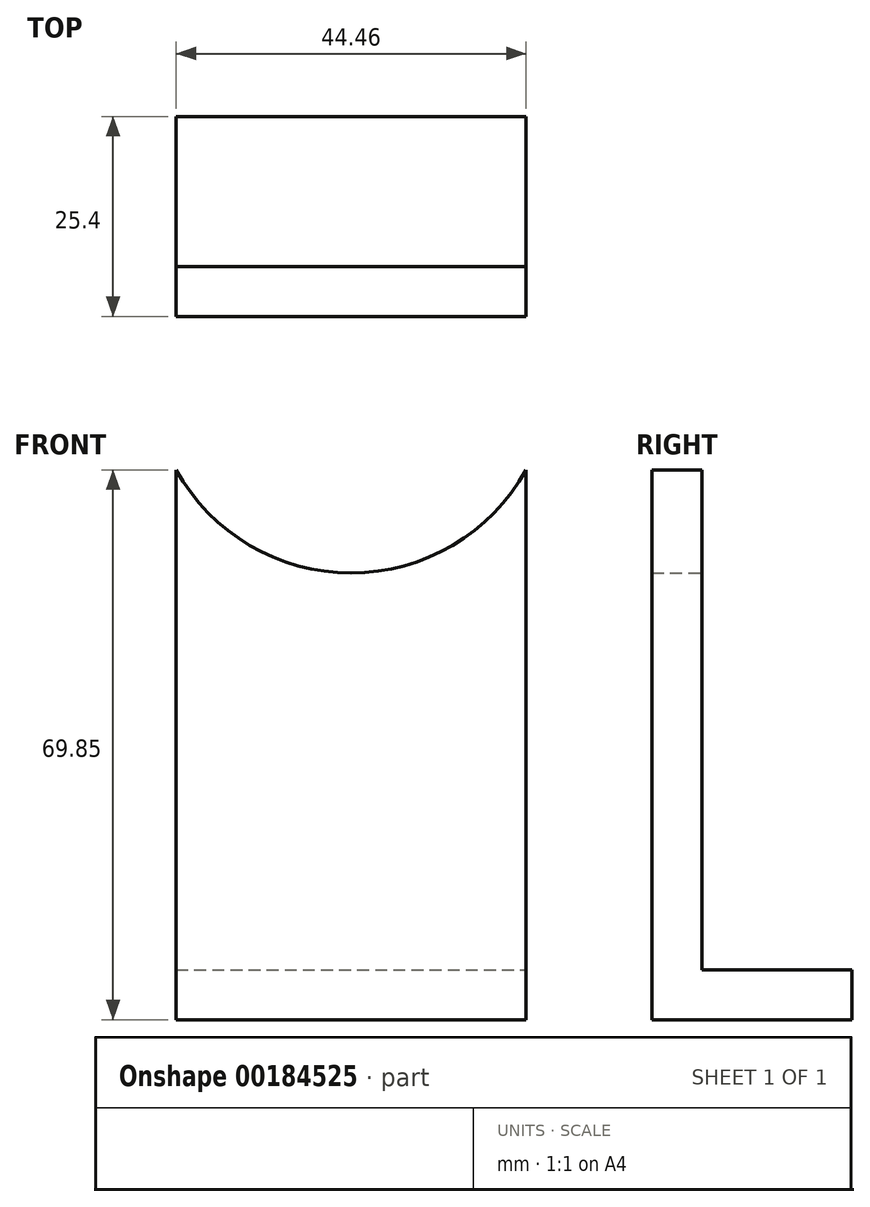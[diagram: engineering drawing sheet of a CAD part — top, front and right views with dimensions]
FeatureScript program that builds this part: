
annotation { "Feature Type Name" : "Feature", "Feature Type Description" : "" }
export const myFeature = defineFeature(function(context is Context, id is Id, definition is map)
    precondition{}
    {
        {
            var Q0;
            Q0=qCreatedBy(makeId("Front.planeOp"),FACE);
            var sketch = newSketch(context, id + "F0", { "sketchPlane" : qUnion([Q0])});
            skLineSegment(sketch, "E0", {"start": v(-22.22, 0) * mm, "end": v(-22.23, 69.85) * mm});
            skLineSegment(sketch, "E1", {"start": v(22.23, 0) * mm, "end": v(22.22, 69.85) * mm});
            skArc(sketch, "E2", {"start": v(-22.23, 69.85) * mm, "mid": v(0, 56.75) * mm, "end": v(22.23, 69.85) * mm});
            skLineSegment(sketch, "E3", {"start": v(-22.22, 0) * mm, "end": v(22.22, 0) * mm});
            skSolve(sketch);
        }
        {
            var Q0;
            Q0=makeQuery(id+"F0.imprint","IMPRINT",FACE,{"disambiguationData":[TD([[makeQuery(id+"F0.imprint","IMPRINT",EDGE,{"derivedFrom":sQuery(id+"F0.wireOp",EDGE,"E0")}),-1.0]])]});
            extrude(context, id + "F1", {"entities" : qUnion([Q0]), "endBound" : BoundingType.SYMMETRIC, "depth" : 6.35 * mm});
        }
        {
            var Q0;
            Q0=makeQuery(id+"F1.opExtrude","SWEPT_FACE",FACE,{"disambiguationData":[OSD([sQuery(id+"F0.wireOp",EDGE,"E3")])]});
            var sketch = newSketch(context, id + "F2", { "sketchPlane" : qUnion([Q0])});
            skLineSegment(sketch, "E4.bottom", {"start": v(-22.22, 3.18) * mm, "end": v(22.23, 3.18) * mm});
            skLineSegment(sketch, "E4.top", {"start": v(-22.22, -22.22) * mm, "end": v(22.23, -22.22) * mm});
            skLineSegment(sketch, "E4.left", {"start": v(-22.22, 3.18) * mm, "end": v(-22.22, -22.22) * mm});
            skLineSegment(sketch, "E4.right", {"start": v(22.23, 3.17) * mm, "end": v(22.23, -22.22) * mm});
            skSolve(sketch);
        }
        {
            var Q0;
            {var subQ0=sQuery(id+"F2.wireOp",EDGE,"E4.top");Q0=makeQuery(id+"F2.imprint","IMPRINT",FACE,{"disambiguationData":[TD([[makeQuery(id+"F2.imprint","IMPRINT",EDGE,{"derivedFrom":subQ0}),1.0]])]});}
            extrude(context, id + "F3", {"entities" : qUnion([Q0]), "operationType" : NewBodyOperationType.ADD, "oppositeDirection" : true, "depth" : 6.35 * mm});
        }
    });
